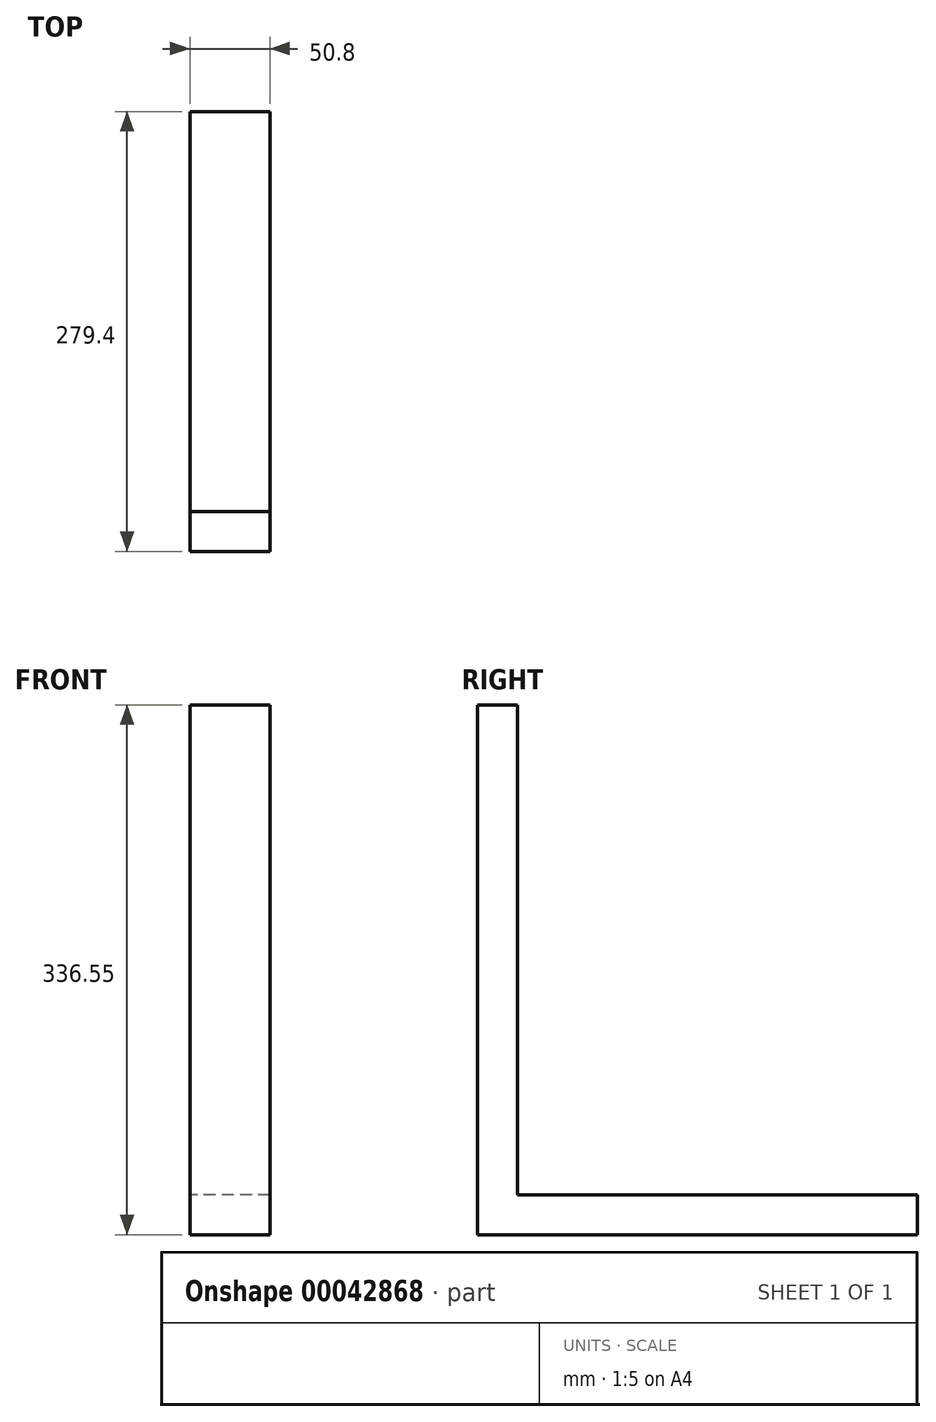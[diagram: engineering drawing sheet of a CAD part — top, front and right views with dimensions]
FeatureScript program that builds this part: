
annotation { "Feature Type Name" : "Feature", "Feature Type Description" : "" }
export const myFeature = defineFeature(function(context is Context, id is Id, definition is map)
    precondition{}
    {
        {
            var Q0;
            Q0=qCreatedBy(makeId("Right.planeOp"),FACE);
            var sketch = newSketch(context, id + "F0", { "sketchPlane" : qUnion([Q0])});
            skLineSegment(sketch, "E0.top", {"start": v(-114.3, -63.5) * mm, "end": v(165.1, -63.5) * mm});
            skLineSegment(sketch, "E0.left", {"start": v(-114.3, 273.05) * mm, "end": v(-114.3, -63.5) * mm});
            skLineSegment(sketch, "E1", {"start": v(-88.9, 273.05) * mm, "end": v(-88.9, -38.1) * mm});
            skLineSegment(sketch, "E2", {"start": v(-88.9, -38.1) * mm, "end": v(165.1, -38.1) * mm});
            skLineSegment(sketch, "E3", {"start": v(-114.3, 273.05) * mm, "end": v(-88.9, 273.05) * mm});
            skLineSegment(sketch, "E4", {"start": v(165.1, -63.5) * mm, "end": v(165.1, -38.1) * mm});
            skSolve(sketch);
        }
        {
            var Q0;
            Q0=makeQuery(id+"F0.imprint","IMPRINT",FACE,{"disambiguationData":[TD([[makeQuery(id+"F0.imprint","IMPRINT",EDGE,{"derivedFrom":sQuery(id+"F0.wireOp",EDGE,"E0.top")}),1.0]])]});
            extrude(context, id + "F1", {"entities" : qUnion([Q0]), "endBound" : BoundingType.SYMMETRIC, "depth" : 50.8 * mm});
        }
    });
